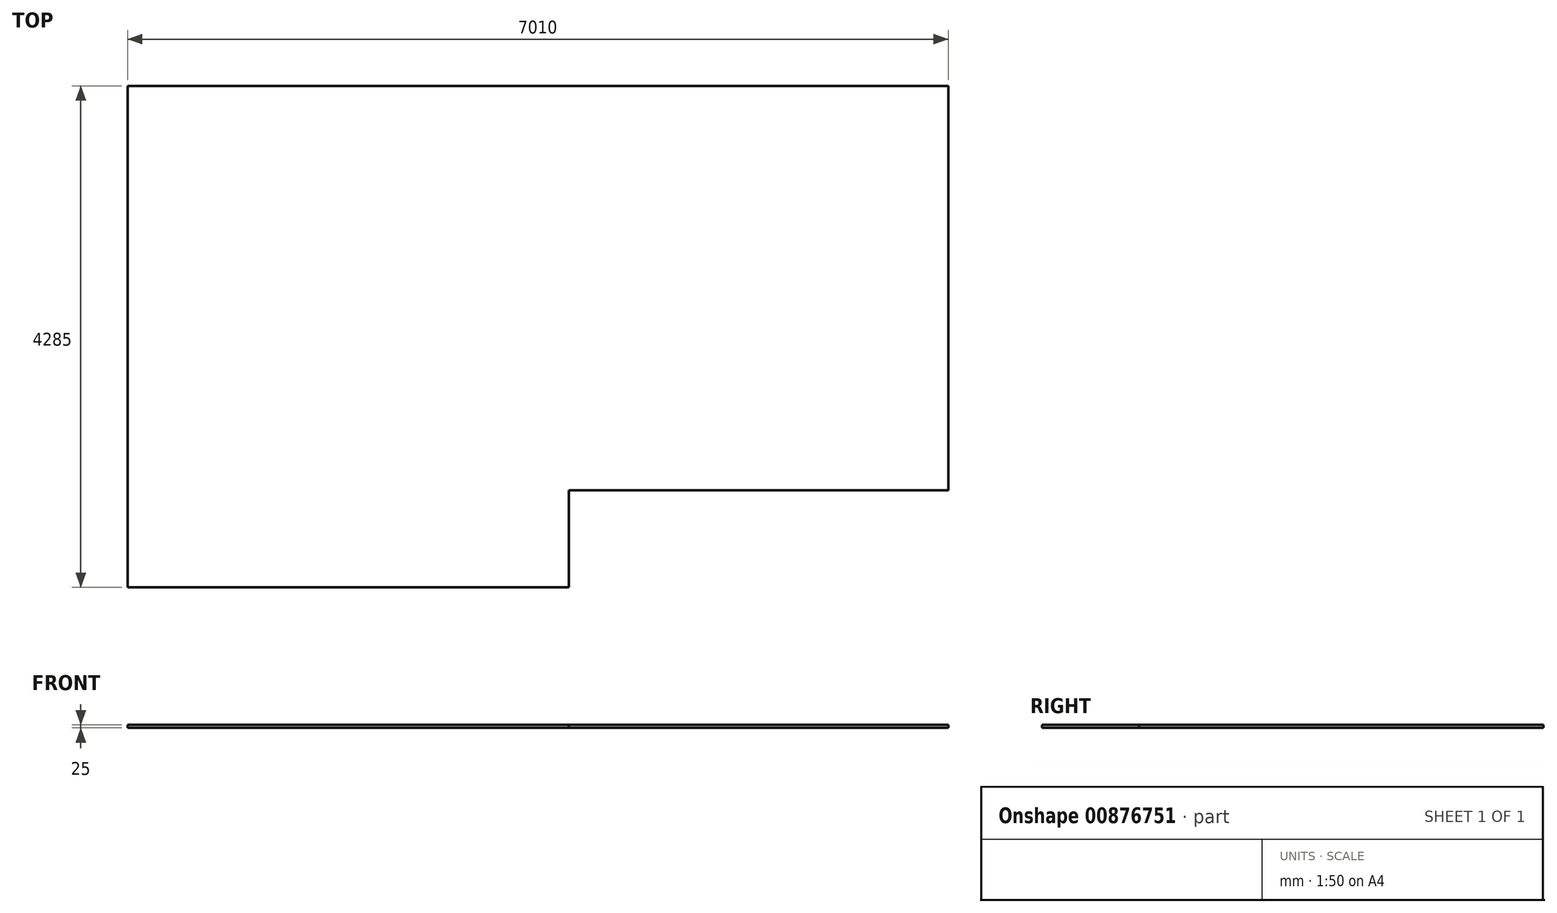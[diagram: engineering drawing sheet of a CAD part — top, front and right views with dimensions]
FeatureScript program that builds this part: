
annotation { "Feature Type Name" : "Feature", "Feature Type Description" : "" }
export const myFeature = defineFeature(function(context is Context, id is Id, definition is map)
    precondition{}
    {
        {
            var Q0;
            Q0=qCreatedBy(makeId("Top.planeOp"),FACE);
            var sketch = newSketch(context, id + "F0", { "sketchPlane" : qUnion([Q0])});
            skLineSegment(sketch, "E0", {"start": v(0, 0) * mm, "end": v(0, -3454) * mm});
            skLineSegment(sketch, "E1", {"start": v(0, 0) * mm, "end": v(-7010, 0) * mm});
            skLineSegment(sketch, "E2", {"start": v(0, -3454) * mm, "end": v(-3239.89, -3454) * mm});
            skLineSegment(sketch, "E3", {"start": v(-3239.89, -3454) * mm, "end": v(-3239.89, -4285) * mm});
            skLineSegment(sketch, "E4", {"start": v(-3239.89, -4285) * mm, "end": v(-7010, -4285) * mm});
            skLineSegment(sketch, "E5", {"start": v(-7010, 0) * mm, "end": v(-7010, -4285) * mm});
            skLineSegment(sketch, "E6", {"start": v(-3962, -4285) * mm, "end": v(-3962, -4763.68) * mm});
            skSolve(sketch);
        }
        {
            var Q0;
            Q0 = qSketchRegion(id + "F0", true);
            extrude(context, id + "F1", {"entities" : qUnion([Q0]), "depth" : 25 * mm, "offsetDistance" : 25 * mm});
        }
    });
